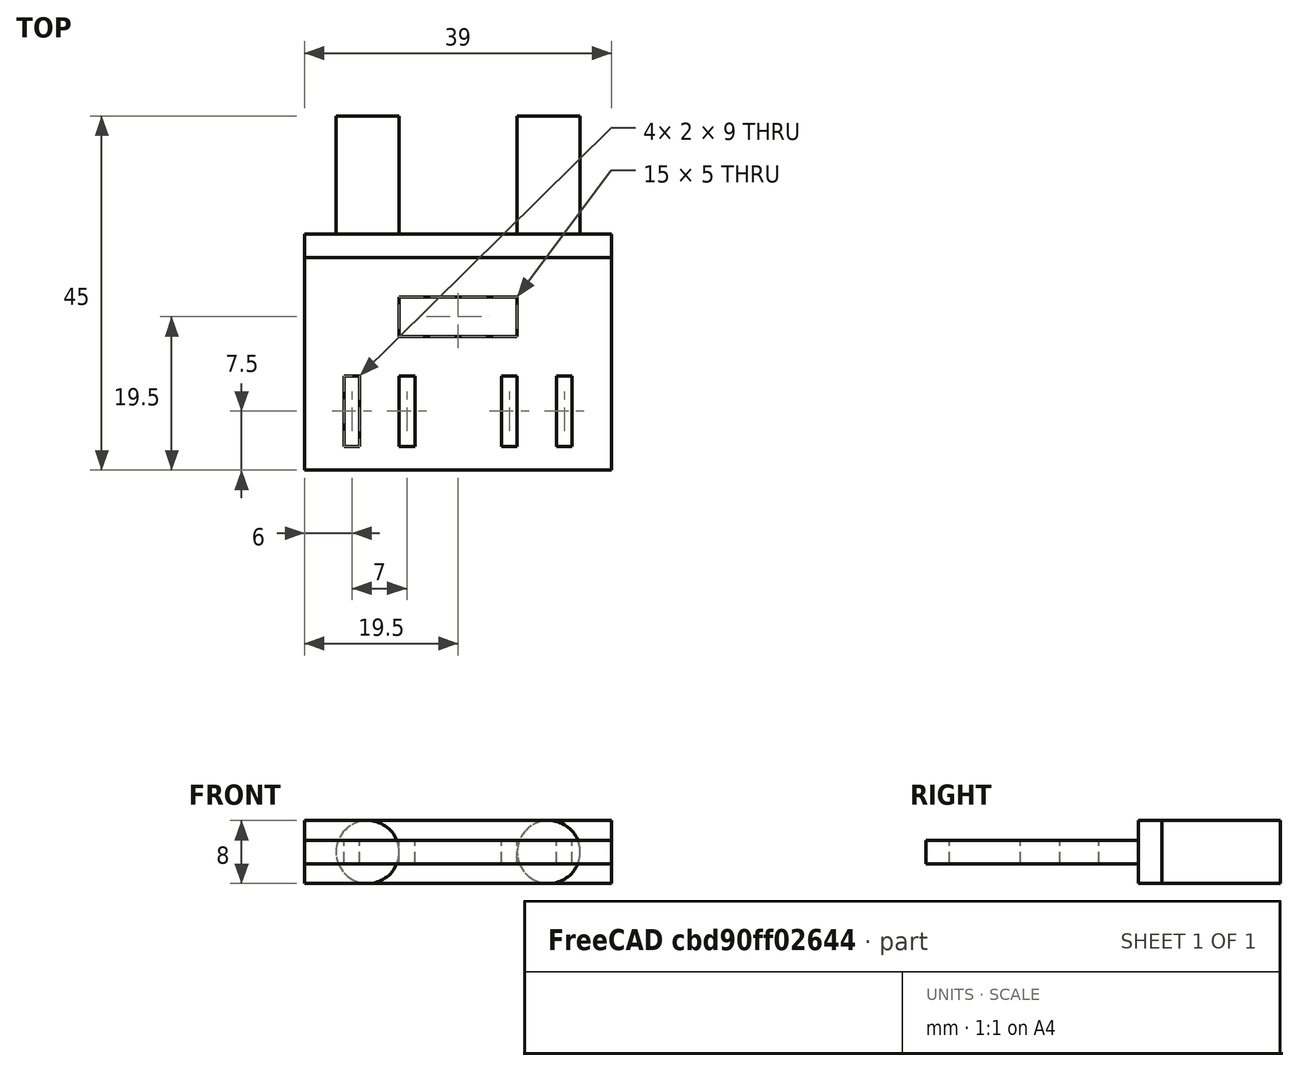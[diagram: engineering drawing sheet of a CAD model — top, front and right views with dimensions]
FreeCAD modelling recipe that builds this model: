
FCSTD DOCUMENT  (FreeCAD 0.15R4671 (Git))
Label: Holder_V4
License: All rights reserved
LicenseURL: http://en.wikipedia.org/wiki/All_rights_reserved
objects: Part::Box×7, Part::Cylinder×2, Part::MultiFuse×1, Part::Cut×1
note: 11 computed .brp shape members not serialized (recipe doc carries the construction recipe); baked Part::Feature solids carry a one-line shape summary decoded from their .brp

FEATURE [Part::Box] Box  label="Base"
  Height = 8
  Length = 39
  Placement = pos=(-8,-18,-4) rot=(0,0,1;0rad)
  Width = 3
FEATURE [Part::Cylinder] Cylinder  label="Pin2"
  Angle = 360
  Height = 15
  Placement = pos=(23,0,0) rot=(1,0,0;1.5708rad)
  Radius = 4
FEATURE [Part::Cylinder] Cylinder001  label="Pin1"
  Angle = 360
  Height = 15
  Placement = pos=(0,0,0) rot=(1,0,0;1.5708rad)
  Radius = 4
FEATURE [Part::Box] Box001  label="Holder"
  Height = 3
  Length = 39
  Placement = pos=(-8,-45,-1.5) rot=(0,0,1;0rad)
  Width = 27
FEATURE [Part::Box] Box002  label="Cut1"
  Height = 3
  Length = 15
  Placement = pos=(4,-28,-1.5) rot=(0,0,1;0rad)
  Width = 5
FEATURE [Part::Box] Box003  label="Cut2"
  Height = 3
  Length = 2
  Placement = pos=(24,-42,-1.5) rot=(0,0,1;0rad)
  Width = 9
FEATURE [Part::Box] Box004  label="Cut003"
  Height = 3
  Length = 2
  Placement = pos=(17,-42,-1.5) rot=(0,0,1;0rad)
  Width = 9
FEATURE [Part::Box] Box005  label="Cut004"
  Height = 3
  Length = 2
  Placement = pos=(4,-42,-1.5) rot=(0,0,1;0rad)
  Width = 9
FEATURE [Part::Box] Box006  label="Cut005"
  Height = 3
  Length = 2
  Placement = pos=(-3,-42,-1.5) rot=(0,0,1;0rad)
  Width = 9
FEATURE [Part::MultiFuse] Fusion
  Shapes = -> [Box002,Box003,Box004,Box005,Box006]
FEATURE [Part::Cut] Cut
  Base = -> Box001
  Tool = -> Fusion
